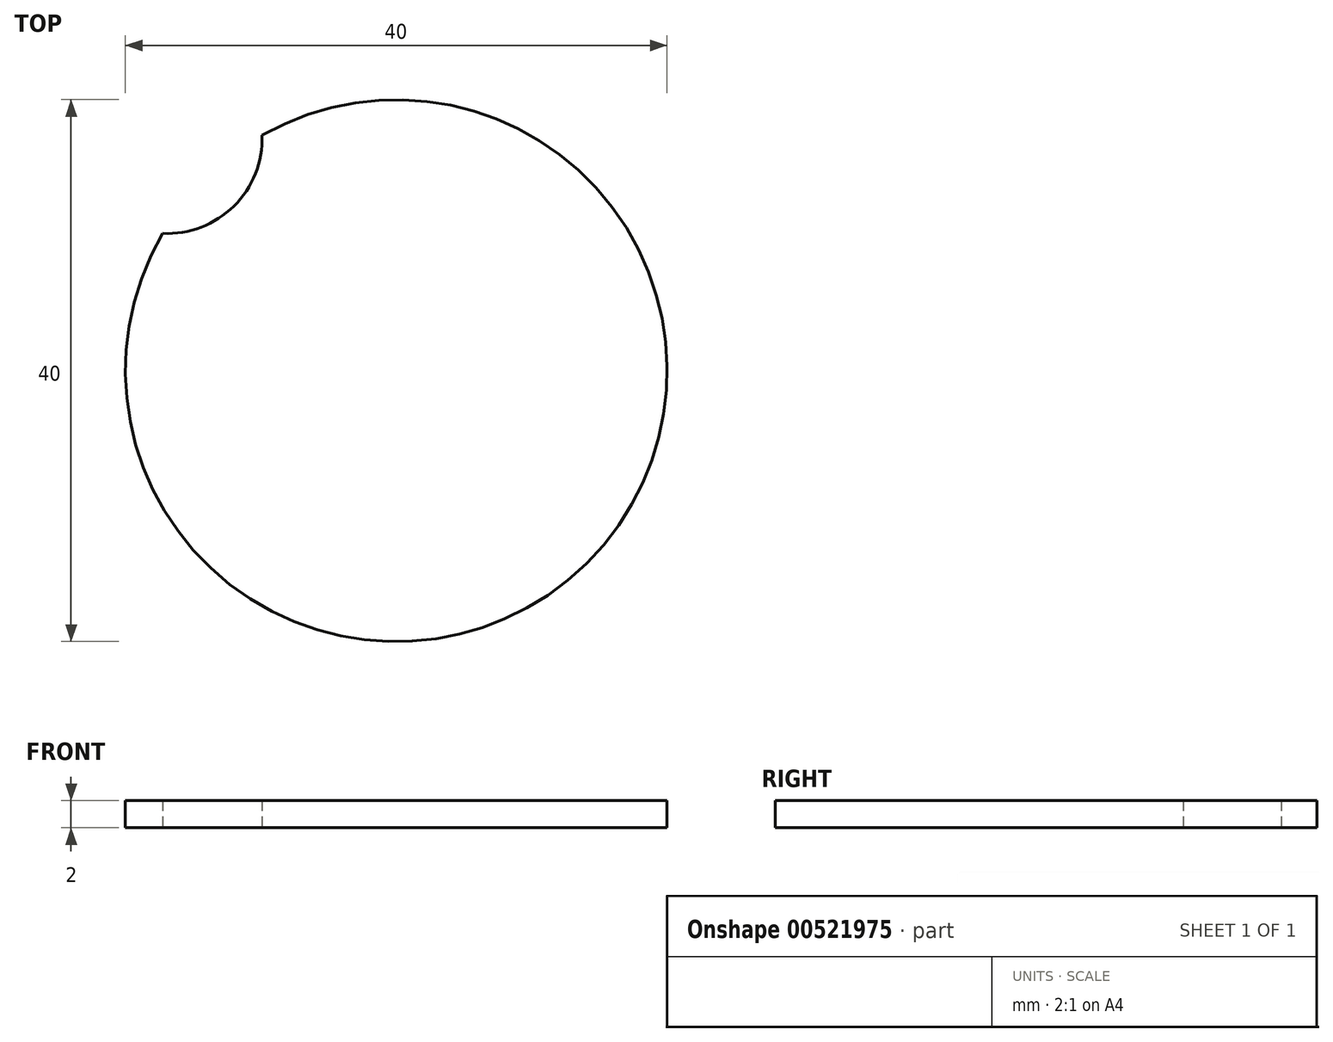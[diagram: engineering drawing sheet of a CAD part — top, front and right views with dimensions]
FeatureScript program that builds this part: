
annotation { "Feature Type Name" : "Feature", "Feature Type Description" : "" }
export const myFeature = defineFeature(function(context is Context, id is Id, definition is map)
    precondition{}
    {
        {
            var Q0;
            Q0=qCreatedBy(makeId("Top.planeOp"),FACE);
            var sketch = newSketch(context, id + "F0", { "sketchPlane" : qUnion([Q0])});
            skCircle(sketch, "E0", {"center": v(-28.87, 19.85) * mm, "radius": 20 * mm});
            skSolve(sketch);
        }
        {
            var Q0;
            Q0 = qSketchRegion(id + "F0", true);
            extrude(context, id + "F1", {"bodyType" : ToolBodyType.SURFACE, "surfaceEntities" : qUnion([Q0]), "depth" : 2 * mm, "offsetDistance" : 25 * mm});
        }
        {
            var Q0;
            Q0=qCreatedBy(makeId("Top.planeOp"),FACE);
            var sketch = newSketch(context, id + "F2", { "sketchPlane" : qUnion([Q0])});
            skCircle(sketch, "E1", {"center": v(-45.79, 36.99) * mm, "radius": 7.01 * mm});
            skSolve(sketch);
        }
        {
            var Q0;
            Q0 = qSketchRegion(id + "F2", true);
            extrude(context, id + "F3", {"entities" : qUnion([Q0]), "operationType" : NewBodyOperationType.REMOVE, "depth" : 25 * mm, "offsetDistance" : 25 * mm});
        }
    });
